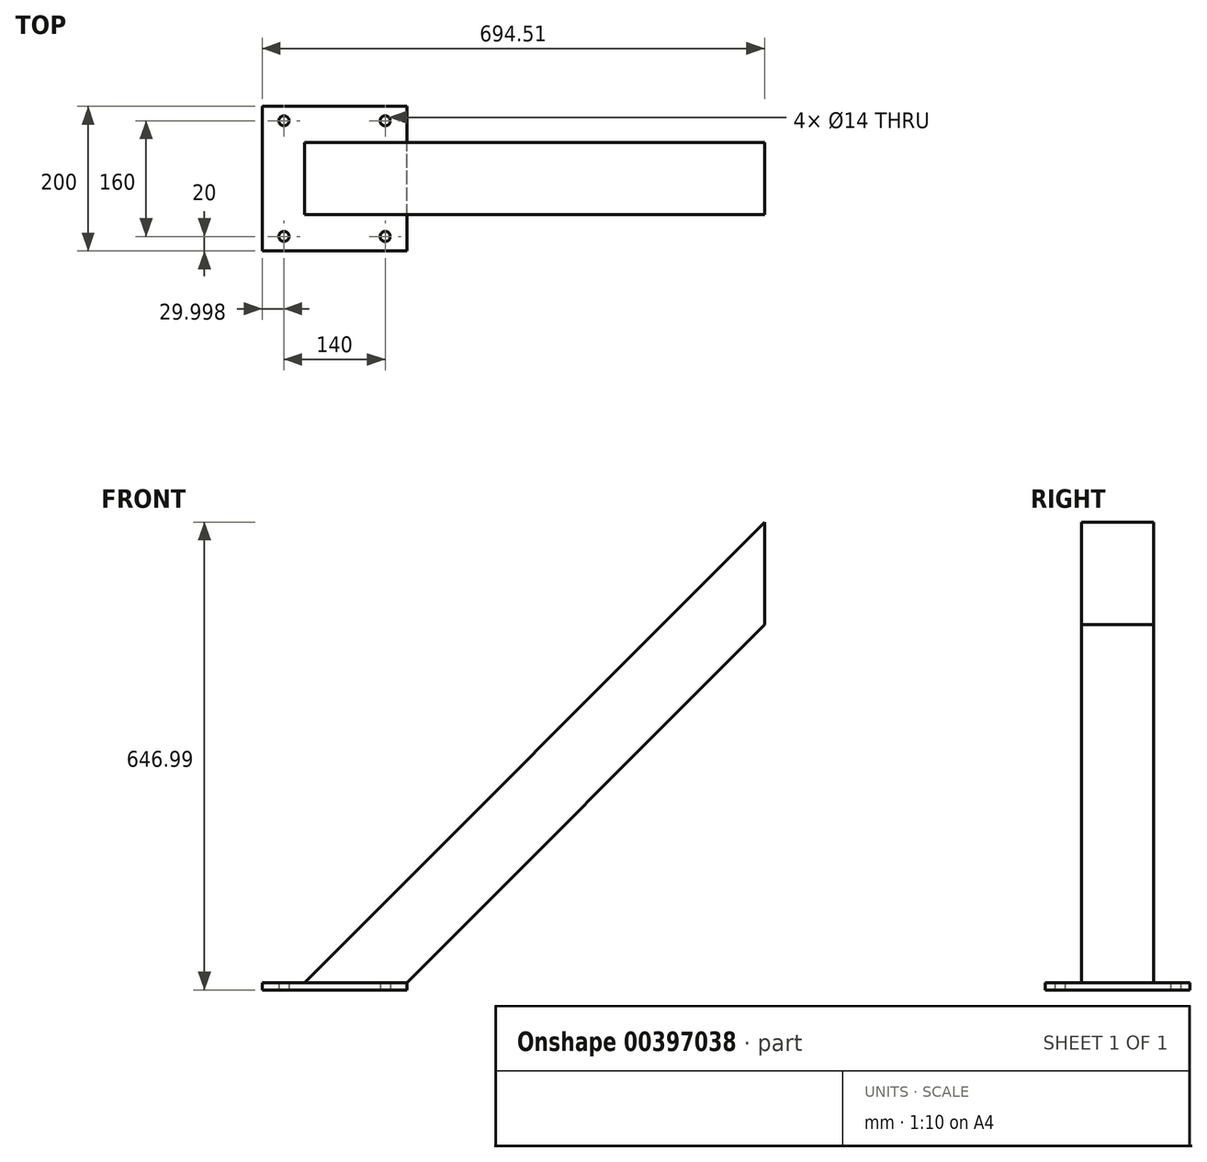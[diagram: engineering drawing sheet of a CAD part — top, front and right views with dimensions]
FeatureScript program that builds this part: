
annotation { "Feature Type Name" : "Feature", "Feature Type Description" : "" }
export const myFeature = defineFeature(function(context is Context, id is Id, definition is map)
    precondition{}
    {
        {
            var Q0;
            Q0=qCreatedBy(makeId("Front.planeOp"),FACE);
            var sketch = newSketch(context, id + "F0", { "sketchPlane" : qUnion([Q0])});
            skLineSegment(sketch, "E0", {"start": v(-70.78, 70.65) * mm, "end": v(-706.58, -566.34) * mm});
            skLineSegment(sketch, "E1", {"start": v(-706.58, -566.34) * mm, "end": v(-565.3, -566.34) * mm});
            skLineSegment(sketch, "E2", {"start": v(-70.78, 70.65) * mm, "end": v(-70.78, -70.9) * mm});
            skLineSegment(sketch, "E3", {"start": v(-70.78, -70.9) * mm, "end": v(-565.3, -566.34) * mm});
            skSolve(sketch);
        }
        {
            var Q0;
            Q0 = qSketchRegion(id + "F0", true);
            extrude(context, id + "F1", {"entities" : qUnion([Q0]), "depth" : 100 * mm});
        }
        {
            var Q0;
            Q0=makeQuery(id+"F1.opExtrude","SWEPT_FACE",FACE,{"disambiguationData":[OSD([sQuery(id+"F0.wireOp",EDGE,"E1")])]});
            var sketch = newSketch(context, id + "F2", { "sketchPlane" : qUnion([Q0])});
            skLineSegment(sketch, "E4", {"start": v(-565.3, 100) * mm, "end": v(-565.3, 150) * mm});
            skPoint(sketch, "E4.endSnap0", {"position": v(-565.3, 50) * mm});
            skLineSegment(sketch, "E5.bottom", {"start": v(-565.3, 150) * mm, "end": v(-765.3, 150) * mm});
            skLineSegment(sketch, "E5.top", {"start": v(-565.3, -50) * mm, "end": v(-765.3, -50) * mm});
            skLineSegment(sketch, "E5.left", {"start": v(-565.3, 150) * mm, "end": v(-565.3, -50) * mm});
            skLineSegment(sketch, "E5.right", {"start": v(-765.3, 150) * mm, "end": v(-765.3, -50) * mm});
            skSolve(sketch);
        }
        {
            var Q0;
            Q0 = qSketchRegion(id + "F2", true);
            extrude(context, id + "F3", {"entities" : qUnion([Q0]), "operationType" : NewBodyOperationType.ADD, "depth" : 10 * mm});
        }
        {
            var Q0;
            Q0=makeQuery(id+"F3.opExtrude","CAP_FACE",FACE,{"disambiguationData":[OSD([sQuery(id+"F2.wireOp",EDGE,"E5.bottom"),sQuery(id+"F2.wireOp",EDGE,"E5.top"),sQuery(id+"F2.wireOp",EDGE,"E5.left"),sQuery(id+"F2.wireOp",EDGE,"E5.right")])],"isStart":false});
            var sketch = newSketch(context, id + "F4", { "sketchPlane" : qUnion([Q0])});
            skLineSegment(sketch, "E6", {"start": v(-765.3, 150) * mm, "end": v(-735.3, 150) * mm});
            skLineSegment(sketch, "E7", {"start": v(-735.3, 150) * mm, "end": v(-735.3, 130) * mm});
            skLineSegment(sketch, "E8", {"start": v(-735.3, 130) * mm, "end": v(-735.3, -30) * mm});
            skLineSegment(sketch, "E9", {"start": v(-735.3, -30) * mm, "end": v(-595.3, -30) * mm});
            skLineSegment(sketch, "E10", {"start": v(-595.3, -30) * mm, "end": v(-595.3, 130) * mm});
            skSolve(sketch);
        }
        {
            var Q0;
            Q0=sQuery(id+"F4.wireOp",VERTEX,"E8.start");
            var Q1;
            Q1=sQuery(id+"F4.wireOp",VERTEX,"E10.end");
            var Q2;
            Q2=sQuery(id+"F4.wireOp",VERTEX,"E10.start");
            var Q3;
            Q3=sQuery(id+"F4.wireOp",VERTEX,"E9.start");
            var Q4;
            Q4=makeQuery(id+"F1.opExtrude","SWEPT_BODY",BODY,{"disambiguationData":[OSD([sQuery(id+"F0.wireOp",EDGE,"E0"),sQuery(id+"F0.wireOp",EDGE,"E1"),sQuery(id+"F0.wireOp",EDGE,"E2"),sQuery(id+"F0.wireOp",EDGE,"E3")])]});
            hole(context, id + "F5", {"style" : HoleStyle.SIMPLE, "endStyle" : HoleEndStyle.BLIND, "holeDiameter" : 14 * mm, "holeDepth" : 150 * mm, "isTappedThrough" : true, "tappedDepth" : 12 * mm, "tapClearance" : 3, "locations" : qUnion([Q0, Q1, Q2, Q3]), "scope" : qUnion([Q4])});
        }
    });
